# Revit family: DSM
name_source: partatom
category: Specialty Equipment
units: mm (PartAtom-declared; Revit-internal decimal feet)

## family parameters
Cut with Voids When Loaded = No
Host = Face
Part Type = Normal
Room Calculation Point = No
Round Connector Dimension = Use Diameter
Shared = No

## types (15) — shared parameters
ABAA Compliance = Yes
Assembly Code = C3020200
Default Elevation = 0' - 0"
Description = Watertight trafficable expansion joint for decks, walkways, ramps and roadways
Durometer Hardness of Silicone Coating (ASTM D2240) = Shore A: 15
Manufacturer = EMSEAL Joint Systems Ltd
Manufacturer URL = http://www.emseal.com
Model = DSM
Movement (of Nominal Material Size) = +50% / -50%
Pick Resistance = No
Product Documentataion URL = https://bit.ly
Product Page URL = https://www.emseal.com
R Value Range (ASTM C518) = 1.8 per 1-inch (25mm) depth
Rate of Air Leakage (ASTM E283) = Passed
Seal Material = Silicone - Sikasil WS-295 Deck Gray
Seal Material Note = DSM is coated on the top traffic side with standard Sikasil WS-295 water-resistant traffic-grade silicone
Staining (ASTM C510) = None
Temperature Range (ASTM C711) = 185°F (85°C) to -40°F (-40°C)
Tensile Strength (ASTM D3574) = 18 psi min; 145 kPa
Type Image = DSM.PNG

## per-type parameters (varying)
| type | Depth | Quad Bellow | Single Bellow | Triple Bellow | Width |
| DSM - .5 inches | 0' - 1 3/4" | No | Yes | No | 0' - 0 1/2" |
| DSM - .75 inches | 0' - 1 3/4" | No | Yes | No | 0' - 0 3/4" |
| DSM - 1 inches | 0' - 2" | No | Yes | No | 0' - 1" |
| DSM - 1.25 inches | 0' - 2" | No | Yes | No | 0' - 1 1/4" |
| DSM - 1.5 inches | 0' - 2 1/2" | No | No | Yes | 0' - 1 1/2" |
| DSM - 1.75 inches | 0' - 2 1/2" | No | No | Yes | 0' - 1 3/4" |
| DSM - 2 inches | 0' - 2 1/2" | No | No | Yes | 0' - 2" |
| DSM - 2.25 inches | 0' - 2 1/2" | No | No | Yes | 0' - 2 1/4" |
| DSM - 2.5inches | 0' - 2 3/4" | No | No | Yes | 0' - 2 1/2" |
| DSM - 2.75 inches | 0' - 3 1/4" | No | No | Yes | 0' - 2 3/4" |
| DSM - 3 inches | 0' - 3 1/4" | No | No | Yes | 0' - 3" |
| DSM - 3.25 inches | 0' - 3 1/2" | Yes | No | No | 0' - 3 1/4" |
| DSM - 3.5 inches | 0' - 3 1/2" | Yes | No | No | 0' - 3 1/2" |
| DSM - 3.75 inches | 0' - 4" | Yes | No | No | 0' - 3 3/4" |
| DSM - 4 inches | 0' - 4" | Yes | No | No | 0' - 4" |

## geometry (parser evidence)
native form markers: Sweep x2
no freeform markers — native parametric forms only
